# Revit family: Gleitlager T HV3, m.D., Ø64 bis Ø219mm (h=151-177mm)
name_source: partatom
category: HLS-Bauteile
units: mm (PartAtom-declared; Revit-internal decimal feet)

## family parameters
Arbeitsebenenbasiert = Ja
Beim Laden mit Abzugskörper schneiden = Nein
Bemaßung runder Anschluss = Durchmesser verwenden
Beschriftungsausrichtung beibehalten = Nein
Gemeinsam genutzt = Ja
Immer vertikal = Nein
Klassifizierung = Keine
Raumberechnungspunkt = Nein
Teiletyp = Normal

## types (13) — shared parameters
Anzahl Rohrschellen = 2
Baustoffklasse = B2
Breite Schellenband = 50 mm
Breite Unterbau = 100 mm
Dämmstärke = 6 mm  [stored 0.019685 ft]
Fabrikat = MEFA
Hersteller = MEFA
Kurztext1 = Gleitlager T 2 RS HV3 50x5
Länge Unterbau = 250 mm
Material = Stahl
Materialname = S235
Mengeneinheit = St
Schalldämmeinlage = Gummi EPDM
Sicherheitsfaktor = 1.54
Stärke Material = 8 mm  [stored 0.0262467 ft]
Stärke Schellenband = 5 mm
Verschluss = Mutter / Verschluss-Schraube
Vorgabe-Ansicht = 1219 mm
max. Höhe Unterbau = 175 mm
max. Temperaturbeständigkeit = 100 °C
min. Höhe Unterbau = 150 mm
vpe = 1
zero-valued in all types: max. Rohraußendurchmesser, min. Rohraußendurchmesser

## per-type parameters (varying)
| type | Artikelnummer | EAN | Gewicht | Gewicht pro Bauteil | Kurztext2 | Nennweite DN Rohr | Rohraußendurchmesser | Schellenteil | max. Rohrachse | min. Rohrachse |
| Gleitlager T HV3, m.2 RS, m.D., Ø 64 (h=151-177mm) | 141cfbb0064 | 4250928461445 | 5.56 kg | 5.56 kg | 64 mm EPDM 100x250 mm fsv | 0 mm  [stored 0 ft] | 64 mm  [stored 0.209974 ft] | TL-141S_b0076 bis 0231, m.D : mit RS Ø64mm m.D | 209 mm | 183 mm |
| Gleitlager T HV3, m.2 RS, m.D., Ø 76 (h=151-177mm) | 141cfbb0076 | 4250928461452 | 5.77 kg | 5.77 kg | 76 mm EPDM 100x250 mm fsv | 65 mm  [stored 0.213255 ft] | 76 mm  [stored 0.249344 ft] | TL-141S_b0076 bis 0231, m.D : mit RS Ø76mm m.D | 215 mm | 189 mm |
| Gleitlager T HV3, m.2 RS, m.D., Ø 89 (h=151-177mm) | 141cfbb0089 | 4250928461469 | 5.97 kg | 5.97 kg | 89 mm EPDM 100x250 mm fsv | 80 mm  [stored 0.262467 ft] | 89 mm  [stored 0.291995 ft] | TL-141S_b0076 bis 0231, m.D : mit RS Ø88.9mm, m.D | 222 mm | 196 mm |
| Gleitlager T HV3, m.2 RS, m.D., Ø108 (h=151-177mm) | 141cfbb0108 | 4250928461476 | 6.27 kg | 6.27 kg | 108 mm EPDM 100x250 mm fsv | 0 mm  [stored 0 ft] | 108 mm  [stored 0.354331 ft] | TL-141S_b0076 bis 0231, m.D : mit RS Ø108mm m.D | 231 mm | 205 mm |
| Gleitlager T HV3, m.2 RS, m.D., Ø110 (h=151-177mm) | 141cfbb0110 | 4250928461483 | 6.30 kg | 6.30 kg | 110 mm EPDM 100x250 mm fsv | 0 mm  [stored 0 ft] | 110 mm  [stored 0.360892 ft] | TL-141S_b0076 bis 0231, m.D : mit RS Ø110mm m.D | 232 mm | 206 mm |
| Gleitlager T HV3, m.2 RS, m.D., Ø114 (h=151-177mm) | 141cfbb0114 | 4250928461490 | 6.37 kg | 6.37 kg | 114 mm EPDM 100x250 mm fsv | 100 mm  [stored 0.328084 ft] | 114 mm  [stored 0.374016 ft] | TL-141S_b0076 bis 0231, m.D : mit RS Ø114.3mm m.D | 234 mm | 208 mm |
| Gleitlager T HV3, m.2 RS, m.D., Ø133 (h=151-177mm) | 141cfbb0133 | 4250928461506 | 6.67 kg | 6.67 kg | 133 mm EPDM 100x250 mm fsv | 0 mm  [stored 0 ft] | 133 mm  [stored 0.436352 ft] | TL-141S_b0076 bis 0231, m.D : mit RS Ø133mm m.D | 244 mm | 218 mm |
| Gleitlager T HV3, m.2 RS, m.D., Ø140 (h=151-177mm) | 141cfbb0140 | 4250928461513 | 6.79 kg | 6.79 kg | 140 mm EPDM 100x250 mm fsv | 125 mm  [stored 0.410105 ft] | 140 mm  [stored 0.459318 ft] | TL-141S_b0076 bis 0231, m.D : mit RS Ø139.7mm m.D | 247 mm | 221 mm |
| Gleitlager T HV3, m.2 RS, m.D., Ø160 (h=151-177mm) | 141cfbb0160 | 4250928461520 | 7.11 kg | 7.11 kg | 160 mm EPDM 100x250 mm fsv | 0 mm  [stored 0 ft] | 160 mm  [stored 0.524934 ft] | TL-141S_b0076 bis 0231, m.D : mit RS Ø160mm m.D | 257 mm | 231 mm |
| Gleitlager T HV3, m.2 RS, m.D., Ø168 (h=151-177mm) | 141cfbb0168 | 4250928461537 | 7.24 kg | 7.24 kg | 168 mm EPDM 100x250 mm fsv | 150 mm  [stored 0.492126 ft] | 168 mm  [stored 0.551181 ft] | TL-141S_b0076 bis 0231, m.D : mit RS Ø168.3mm m.D | 261 mm | 235 mm |
| Gleitlager T HV3, m.2 RS, m.D., Ø180 (h=151-177mm) | 141cfbb0180 | 4250928461544 | 7.43 kg | 7.43 kg | 180 mm EPDM 100x250 mm fsv | 0 mm  [stored 0 ft] | 180 mm  [stored 0.590551 ft] | TL-141S_b0076 bis 0231, m.D : mit RS Ø180mm m.D | 267 mm | 241 mm |
| Gleitlager T HV3, m.2 RS, m.D., Ø210 (h=151-177mm) | 141cfbb0210 | 4250928461551 | 7.91 kg | 7.91 kg | 210 mm EPDM 100x250 mm fsv | 0 mm  [stored 0 ft] | 210 mm  [stored 0.688976 ft] | TL-141S_b0076 bis 0231, m.D : mit RS Ø210mm m.D | 282 mm | 256 mm |
| Gleitlager T HV3, m.2 RS, m.D., Ø219 (h=151-177mm) | 141cfbb0219 | 4250928461568 | 8.05 kg | 8.05 kg | 219 mm EPDM 100x250 mm fsv | 200 mm  [stored 0.656168 ft] | 219 mm  [stored 0.718504 ft] | TL-141S_b0076 bis 0231, m.D : mit RS Ø219mm m.D | 287 mm | 261 mm |

note: [stored X ft] marks values corroborated as IEEE doubles in the binary element streams (Revit-internal decimal feet)

## geometry (parser evidence)
native form markers: Sweep x8
no freeform markers — native parametric forms only
